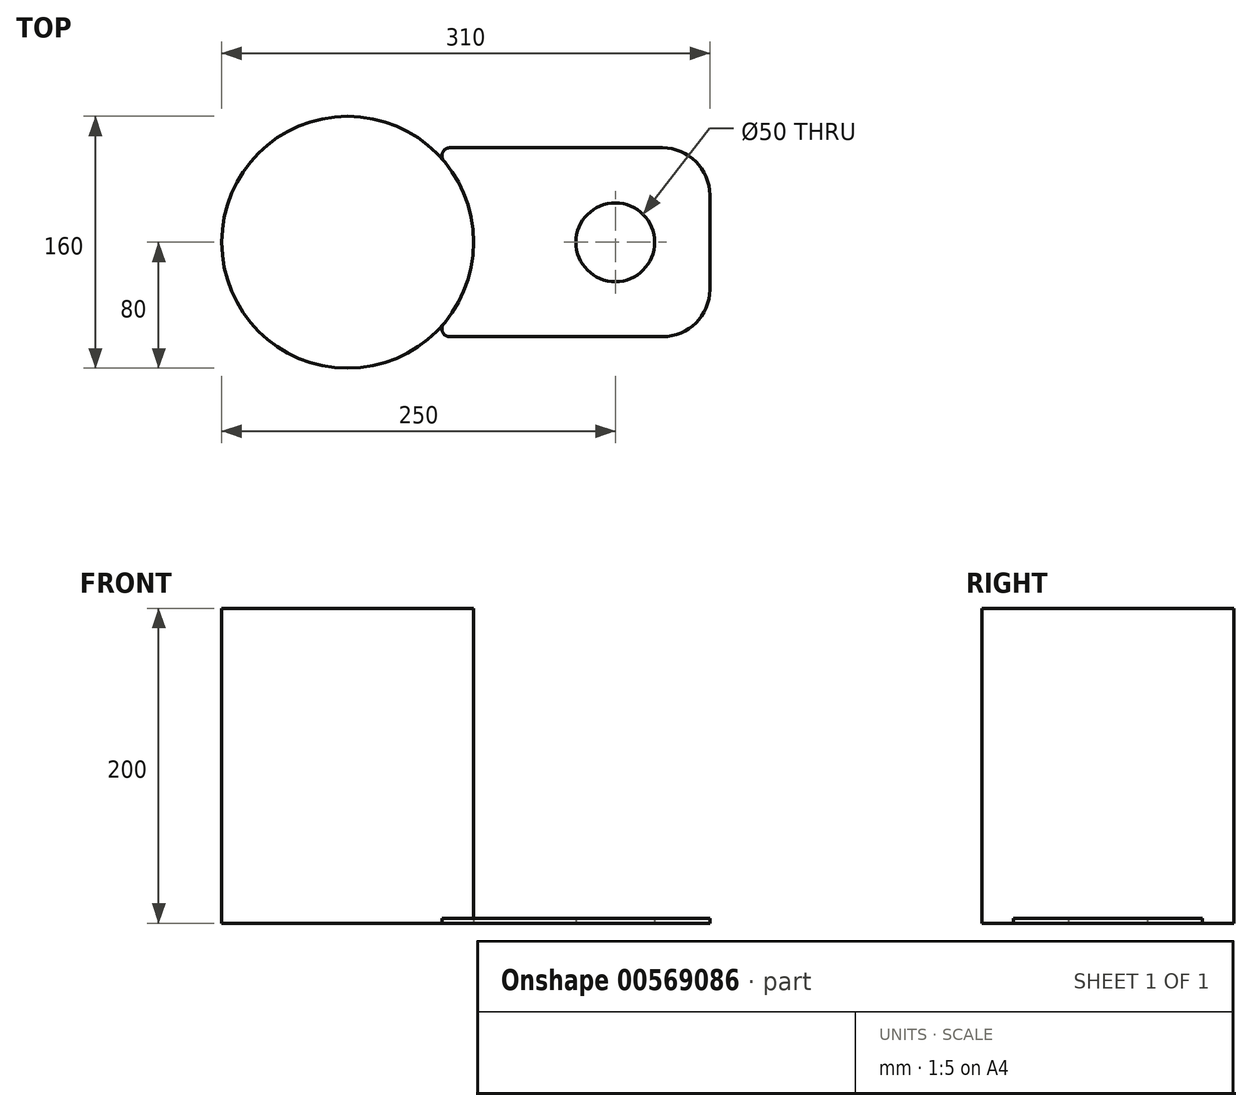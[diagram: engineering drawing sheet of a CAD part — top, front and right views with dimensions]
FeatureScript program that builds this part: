
annotation { "Feature Type Name" : "Feature", "Feature Type Description" : "" }
export const myFeature = defineFeature(function(context is Context, id is Id, definition is map)
    precondition{}
    {
        {
            var Q0;
            Q0=qCreatedBy(makeId("Top.planeOp"),FACE);
            var sketch = newSketch(context, id + "F0", { "sketchPlane" : qUnion([Q0])});
            skCircle(sketch, "E0", {"center": v(0, 0) * mm, "radius": 80 * mm});
            skSolve(sketch);
        }
        {
            var Q0;
            Q0 = qSketchRegion(id + "F0", true);
            extrude(context, id + "F1", {"entities" : qUnion([Q0]), "depth" : 200 * mm, "offsetDistance" : 25 * mm});
        }
        {
            var Q0;
            Q0=qCreatedBy(makeId("Top.planeOp"),FACE);
            var sketch = newSketch(context, id + "F2", { "sketchPlane" : qUnion([Q0])});
            skLineSegment(sketch, "E1", {"start": v(0, 0) * mm, "end": v(170, 0) * mm, "construction": true});
            skLineSegment(sketch, "E2", {"start": v(64.8, 60) * mm, "end": v(200, 60) * mm});
            skLineSegment(sketch, "E3", {"start": v(230, 30) * mm, "end": v(230, -30) * mm});
            skLineSegment(sketch, "E4", {"start": v(200, -60) * mm, "end": v(64.8, -60) * mm});
            skArc(sketch, "E5", {"start": v(61, -51.76) * mm, "mid": v(80, 0) * mm, "end": v(61, 51.76) * mm});
            skCircle(sketch, "E6", {"center": v(170, 0) * mm, "radius": 25 * mm});
            skPoint(sketch, "E7.visualSharp", {"position": v(230, -60) * mm});
            skArc(sketch, "E7.filletArc", {"start": v(200, -60) * mm, "mid": v(221.21, -51.21) * mm, "end": v(230, -30) * mm});
            skPoint(sketch, "E8.visualSharp", {"position": v(230, 60) * mm});
            skArc(sketch, "E8.filletArc", {"start": v(230, 30) * mm, "mid": v(221.21, 51.21) * mm, "end": v(200, 60) * mm});
            skPoint(sketch, "E9.visualSharp", {"position": v(52.92, -60) * mm});
            skArc(sketch, "E9.filletArc", {"start": v(61, -51.76) * mm, "mid": v(60.27, -57.1) * mm, "end": v(64.8, -60) * mm});
            skPoint(sketch, "E10.visualSharp", {"position": v(52.92, 60) * mm});
            skArc(sketch, "E10.filletArc", {"start": v(64.8, 60) * mm, "mid": v(60.27, 57.1) * mm, "end": v(61, 51.76) * mm});
            skSolve(sketch);
        }
        {
            var Q0;
            Q0=makeQuery(id+"F2.imprint","IMPRINT",FACE,{"disambiguationData":[TD([[makeQuery(id+"F2.imprint","IMPRINT",EDGE,{"derivedFrom":sQuery(id+"F2.wireOp",EDGE,"E2")}),-1.0]])]});
            extrude(context, id + "F3", {"entities" : qUnion([Q0]), "depth" : 3 * mm, "offsetDistance" : 25 * mm});
        }
    });
